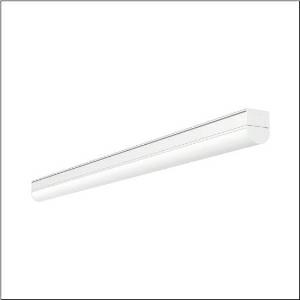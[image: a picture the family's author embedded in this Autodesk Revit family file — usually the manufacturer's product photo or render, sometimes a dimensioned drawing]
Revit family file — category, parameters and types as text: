
# Revit family: ecopack_r__31_51lj12mnm70a_41d1
name_source: partatom
category: Lighting Fixtures
units: mm (PartAtom-declared; Revit-internal decimal feet)

## family parameters
Cut with Voids When Loaded = No
Host = Face
Light Source = No
Part Type = Normal
Room Calculation Point = No
Round Connector Dimension = Use Diameter
Shared = No

## types (1)
- --- (1 x LED, 6780 lm, 50 W, 5000K)
    Apparent Load = 50 VA
    CIE Flux Codes = 39 67 87 89 100
    Color Rendering = 80
    Color Temperature = 5000K
    Default Elevation = 1800 mm
    Description = Ecopack® 31, diffuser luminaire, primary optical cover: cover, of PC, frosted, light emission: direct distribution, primary light characteristic: symmetric, installation type: surface-mounted, LED, rated luminous flux: 7.000lm, luminous efficacy: 140lm/W, light colour: 830/840/850, colour temperature: 3000/4000/5000K, control gear: ON/OFF Multilumen, with terminal, 3-pole, mains connection: 220..240V, AC, 50/60Hz, rated input power: 50W, housing, of aluminium, traffic white (RAL 9016), length: 1.450mm, width: 56mm, height: 68mm, end cap, of PC, white, protection rating (complete): IP20, insulation class (complete): insulation class I (protective earthing), certification: CE, impact resistance: IK06, permissible operating ambient temperature: -20..+40°C, packaging unit: 1 piece
    Height = 68 mm
    Lamp = 1 x LED
    Lamp Light Flux = 6780 lm
    Lamp Power = 50 W
    Lamp count = 1
    Length = 1450 mm
    Luminous efficacy = 136 lm/W
    Manufacturer = Siteco
    ModVariant = No
    Model = 51LJ12MNM70A
    Mounting Place = Ceiling
    Mounting Type = Surface mounted
    Number of Poles = 1
    OnlyDefault = Yes
    Power Factor = 1
    Product Name = Ecopack® 31
    Product group = diffuser luminaire
    ProductGroupID = 307
    Protection Class = Protection class I
    Protection Degree = IP 20
    RLX_Detail_Level = 1
    RLX_Emergency_Light_Flux = 0 lm
    RLX_Emergency_Type = 0
    RLX_Emergency_Type_DB = No
    RlxData = <blob elided: 25469 chars, md5=7c1849b4>
    Socket = socket
    Standby Power = 0 W
    System Light Flux = 6780 lm
    System Power = 50 W
    Type Comments = individual setting: colour temperature 5000K, luminous flux: 100 % | (ON | ON)
    Type Image = l_1007033.jpg
    URL = http://relux.com
    VarID = @adj_195447
    Voltage = 0 V
    Weight = 0.00 kg
    Width = 56 mm

## geometry (parser evidence)
native form markers: Blend x4, Sweep x15
no freeform markers — native parametric forms only
